# Revit family: IEK_R19_L2(2)_Шкаф_ЩРв_IP31_TITAN5_Встроенный
name_source: partatom
category: Электрооборудование
units: mm (PartAtom-declared; Revit-internal decimal feet)

## family parameters
Всегда вертикально = Да
На основе рабочей плоскости = Нет
Общий = Нет
При загрузке вырезать с полостями = Нет
Размер круглого соединителя = Использовать диаметр
Тип детали = Силовой щит
Точка расчета площади = Да

## types (1)
- IEK_R19_L2(2)_Шкаф_ЩРв_IP31_TITAN5_Встроенный
    ADSK_Версия Revit = 2019
    ADSK_Версия семейства = v1.1 2023-03-20
    ADSK_Группирование = Продукция НКУ
    ADSK_Единица измерения = шт
    ADSK_Завод-изготовитель = IEK
    ADSK_Количество = 1
    ADSK_Марка = ЩРв
    ADSK_Масса = 0
    ADSK_Наименование = Щит распределительный встроенной установки IP31
    ADSK_Обозначение = ЩРв
    ADSK_Размер_Высота = 365 мм
    ADSK_Размер_Глубина = 130 мм
    ADSK_Размер_Ширина = 350 мм
    mS_Guid = 821c7fcf-6e20-4866-bf76-5fe537ee1ddb
    mS_Координация оборудования = 0
    Группировать в спецификации = Нет
    Инженерная_сеть = Нет
